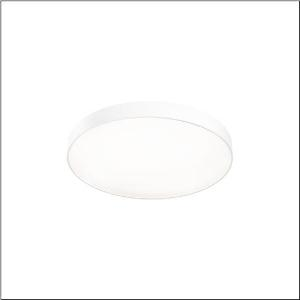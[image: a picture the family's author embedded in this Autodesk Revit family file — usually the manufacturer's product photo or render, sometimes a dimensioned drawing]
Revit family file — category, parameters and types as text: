
# Revit family: round_21_m_51mr36gm8321w
name_source: partatom
category: Lighting Fixtures
units: mm (PartAtom-declared; Revit-internal decimal feet)

## family parameters
Cut with Voids When Loaded = No
Host = Face
Light Source = No
Part Type = Normal
Room Calculation Point = No
Round Connector Dimension = Use Diameter
Shared = No

## types (1)
- --- (1 x LED, 7820 lm, 60.8 W, 3000K)
    Apparent Load = 61 VA
    CIE Flux Codes = 49 80 96 85 100
    Color Rendering = 80
    Color Temperature = 3000K
    Default Elevation = 1800 mm
    Description = Round 21 M, wall and ceiling luminaire, primary optical cover: cover, of PMMA, opal, light emission: direct/indirect distribution, primary light characteristic: symmetric, installation type: suspended mounting, surface-mounted, LED, rated luminous flux: 7.820lm, luminous efficacy: 129lm/W, light colour: 830, colour temperature: 3000K, with terminal, 3-pole, mains connection: 230V, AC, 50/60Hz, rated input power: 61W, housing, of aluminium, coated, white, diameter: 600mm, height: 62mm, protection rating (complete): IP40, insulation class (complete): insulation class I (protective earthing), certification: CE, impact resistance: IK04, permissible operating ambient temperature: -10..+35°C, packaging unit: 1 piece
    Height = 87 mm
    Lamp = 1 x LED
    Lamp Light Flux = 7820 lm
    Lamp Power = 60.8 W
    Lamp count = 1
    Length = 600 mm
    Luminous efficacy = 129 lm/W
    Manufacturer = Siteco
    ModVariant = No
    Model = 51MR36GM8321W
    Mounting Place = Ceiling
    Mounting Type = Surface mounted
    Number of Poles = 1
    OnlyDefault = Yes
    Power Factor = 1
    Product Name = Round 21 M
    Product group = wall and ceiling luminaire
    ProductGroupID = 302
    Protection Class = Protection class I
    Protection Degree = IP 40
    RLX_Detail_Level = 1
    RLX_Emergency_Light_Flux = 0 lm
    RLX_Emergency_Type = 0
    RLX_Emergency_Type_DB = No
    RlxData = <blob elided: 14753 chars, md5=60010c24>
    Socket = socket
    Standby Power = 0 W
    System Light Flux = 7820 lm
    System Power = 61 W
    Type Comments = factory setting: luminous flux: 100 % | (ON | ON | ON | ON) | 700 mA
    Type Image = l_1258330.jpg
    URL = http://relux.com
    VarID = @adj_031887
    Voltage = 0 V
    Weight = 0.00 kg
    Width = 0 mm  [stored 0 ft]

note: [stored X ft] marks values corroborated as IEEE doubles in the binary element streams (Revit-internal decimal feet)

## geometry (parser evidence)
native form markers: Sweep x13
no freeform markers — native parametric forms only
